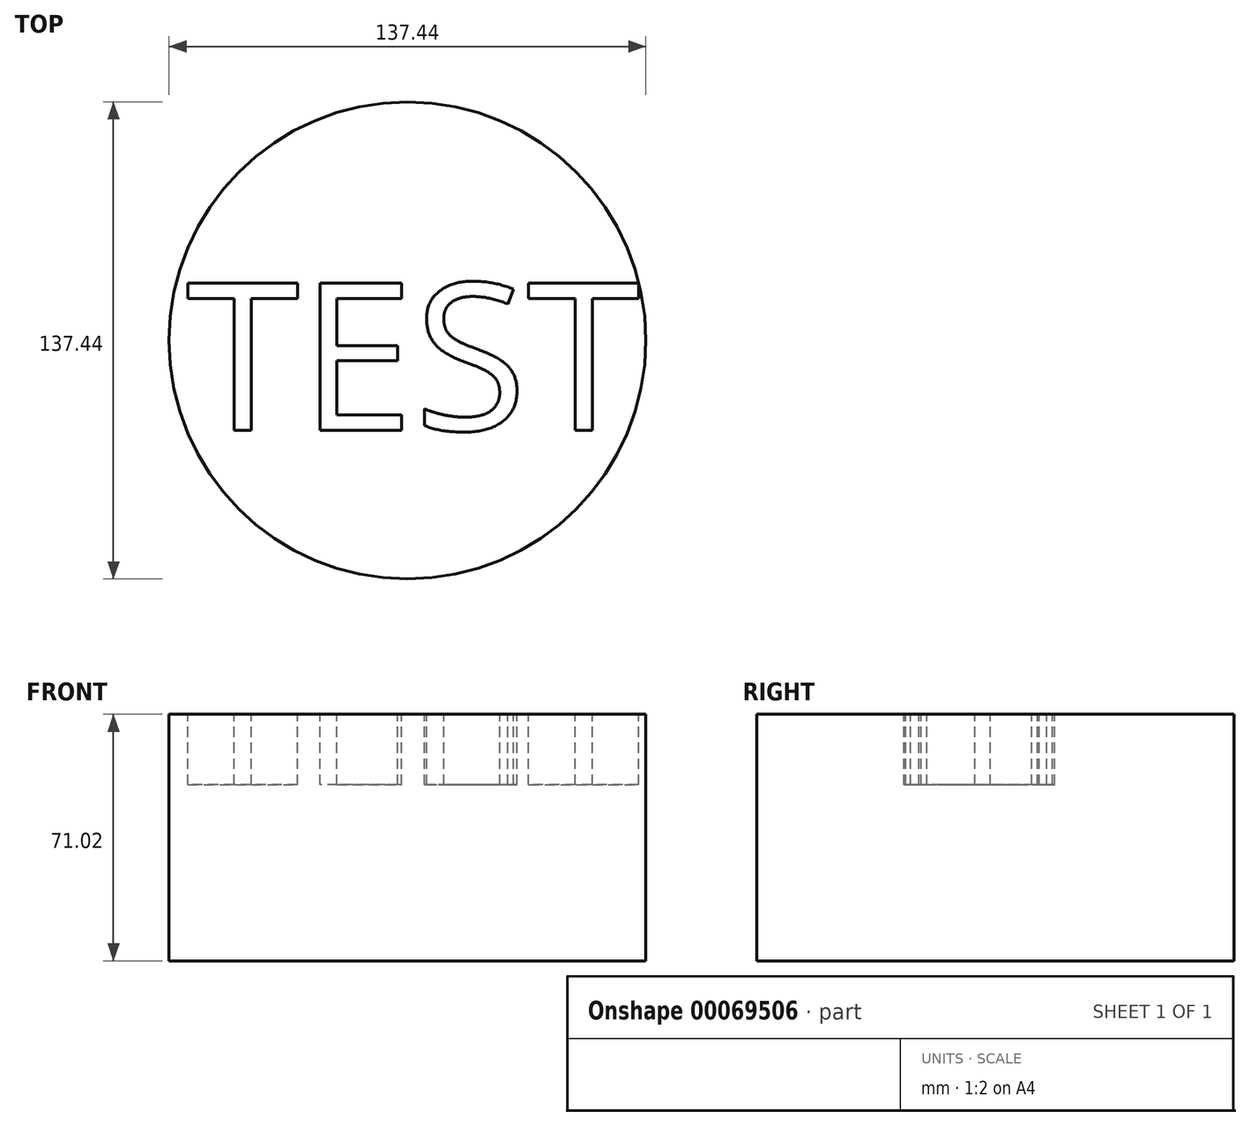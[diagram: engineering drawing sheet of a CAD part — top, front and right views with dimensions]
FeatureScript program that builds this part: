
annotation { "Feature Type Name" : "Feature", "Feature Type Description" : "" }
export const myFeature = defineFeature(function(context is Context, id is Id, definition is map)
    precondition{}
    {
        {
            var Q0;
            Q0=qCreatedBy(makeId("Top.planeOp"),FACE);
            var sketch = newSketch(context, id + "F0", { "sketchPlane" : qUnion([Q0])});
            skCircle(sketch, "E0", {"center": v(0, 0) * mm, "radius": 68.72 * mm});
            skSolve(sketch);
        }
        {
            var Q0;
            Q0=makeQuery(id+"F0.imprint","IMPRINT",FACE,{"disambiguationData":[TD([[makeQuery(id+"F0.imprint","IMPRINT",EDGE,{"derivedFrom":sQuery(id+"F0.wireOp",EDGE,"E0")}),1.0]])]});
            extrude(context, id + "F1", {"entities" : qUnion([Q0]), "depth" : 71.02 * mm});
        }
        {
            var Q0;
            Q0=makeQuery(id+"F1.opExtrude","CAP_FACE",FACE,{"disambiguationData":[OSD([sQuery(id+"F0.wireOp",EDGE,"E0")])],"isStart":false});
            var sketch = newSketch(context, id + "F2", { "sketchPlane" : qUnion([Q0])});
            skText(sketch, "E1", { "text": "TEST", "fontName": "OpenSans-Regular.ttf"});
            const initialGuessF2  = {"E1": [-0.06385, -0.02582, 1, 0, 0.04266]};
            skSetInitialGuess(sketch, initialGuessF2);
            skSolve(sketch);
        }
        {
            var Q0;
            Q0 = qSketchRegion(id + "F2", true);
            extrude(context, id + "F3", {"entities" : qUnion([Q0]), "operationType" : NewBodyOperationType.REMOVE, "oppositeDirection" : true, "depth" : 20.32 * mm});
        }
    });
